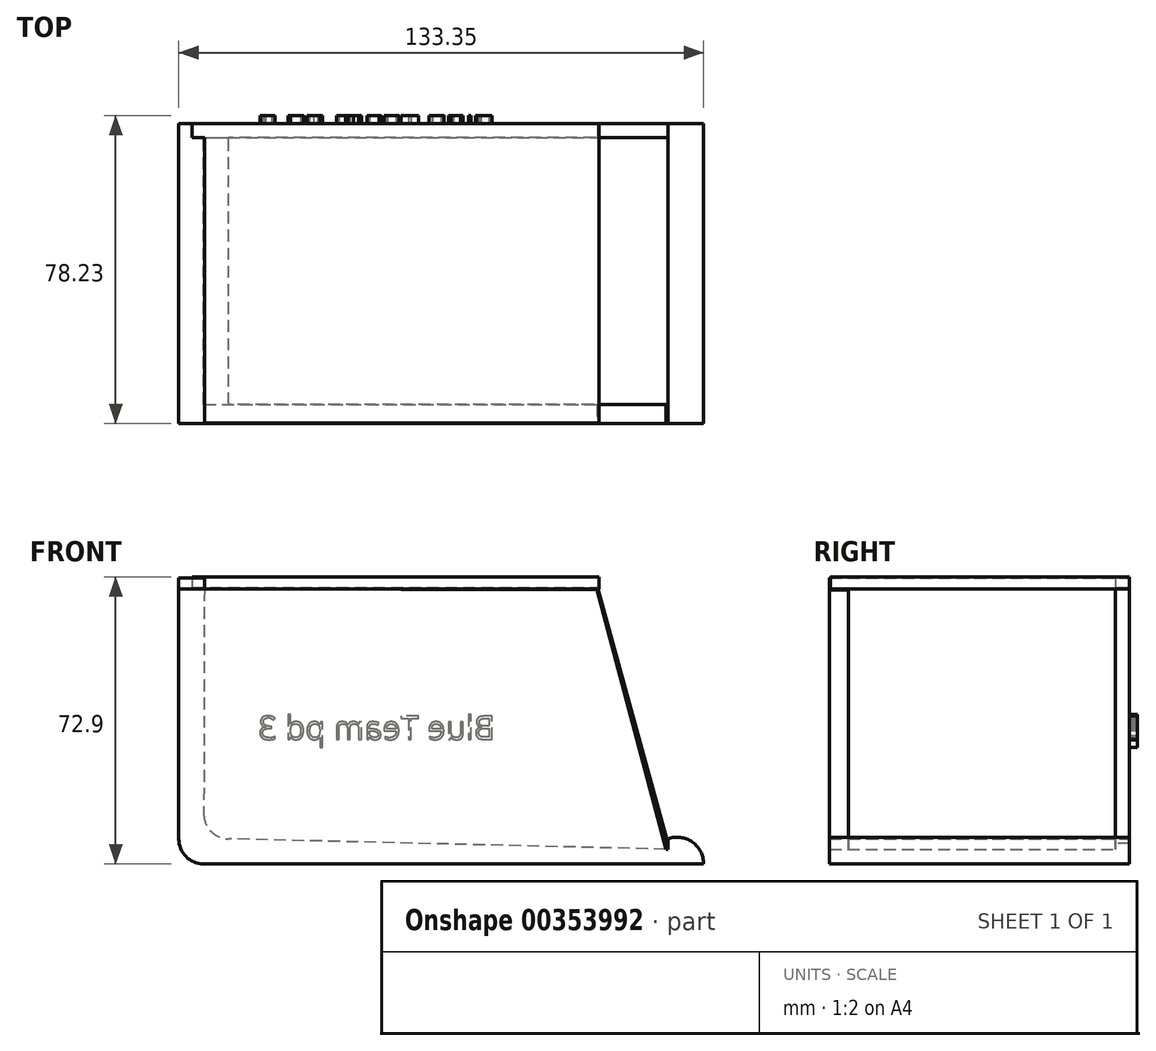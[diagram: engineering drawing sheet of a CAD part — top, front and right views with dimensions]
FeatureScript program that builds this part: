
annotation { "Feature Type Name" : "Feature", "Feature Type Description" : "" }
export const myFeature = defineFeature(function(context is Context, id is Id, definition is map)
    precondition{}
    {
        {
            var Q0;
            Q0=qCreatedBy(makeId("Front.planeOp"),FACE);
            var sketch = newSketch(context, id + "F0", { "sketchPlane" : qUnion([Q0])});
            skLineSegment(sketch, "E0", {"start": v(-20.46, 51.98) * mm, "end": v(-20.46, -11.52) * mm});
            skLineSegment(sketch, "E1", {"start": v(-14.1, -17.87) * mm, "end": v(112.9, -17.87) * mm});
            skPoint(sketch, "E2.visualSharp", {"position": v(-20.46, -17.87) * mm});
            skArc(sketch, "E2.filletArc", {"start": v(-20.46, -11.52) * mm, "mid": v(-18.6, -16) * mm, "end": v(-14.1, -17.87) * mm});
            skLineSegment(sketch, "E3", {"start": v(-20.46, 51.98) * mm, "end": v(-13.95, 51.98) * mm});
            skLineSegment(sketch, "E4", {"start": v(-13.95, 51.98) * mm, "end": v(-14.1, -5.15) * mm});
            skLineSegment(sketch, "E5", {"start": v(112.9, -17.87) * mm, "end": v(112.9, -17.87) * mm});
            skArc(sketch, "E6.filletArc", {"start": v(-14.1, -5.15) * mm, "mid": v(-12.24, -9.65) * mm, "end": v(-7.74, -11.52) * mm});
            skArc(sketch, "E7", {"start": v(112.9, -17.87) * mm, "mid": v(110, -12.31) * mm, "end": v(103.78, -11.52) * mm});
            skLineSegment(sketch, "E8", {"start": v(103.78, -11.52) * mm, "end": v(103.78, -14.16) * mm});
            skLineSegment(sketch, "E9", {"start": v(103.78, -14.16) * mm, "end": v(-7.74, -11.52) * mm});
            skLineSegment(sketch, "E10", {"start": v(-13.95, 51.98) * mm, "end": v(60.84, 51.8) * mm});
            skLineSegment(sketch, "E11", {"start": v(60.84, 51.8) * mm, "end": v(83.04, 51.8) * mm});
            skLineSegment(sketch, "E12", {"start": v(83.04, 51.8) * mm, "end": v(103.78, -11.52) * mm});
            skSolve(sketch);
        }
        {
            var Q0;
            Q0=makeQuery(id+"F0.imprint","IMPRINT",FACE,{"disambiguationData":[TD([[makeQuery(id+"F0.imprint","IMPRINT",EDGE,{"derivedFrom":sQuery(id+"F0.wireOp",EDGE,"E0")}),1.0]])]});
            extrude(context, id + "F1", {"entities" : qUnion([Q0]), "depth" : 76.2 * mm});
        }
        {
            var Q0;
            Q0=qCreatedBy(makeId("Front.planeOp"),FACE);
            var sketch = newSketch(context, id + "F2", { "sketchPlane" : qUnion([Q0])});
            skLineSegment(sketch, "E13", {"start": v(-17.13, 52.33) * mm, "end": v(86, 52.33) * mm});
            skLineSegment(sketch, "E14", {"start": v(86, 52.33) * mm, "end": v(104.33, -14.69) * mm});
            skLineSegment(sketch, "E15", {"start": v(104.33, -14.69) * mm, "end": v(-17.06, -13.08) * mm});
            skLineSegment(sketch, "E16", {"start": v(-17.06, -13.08) * mm, "end": v(-17.13, 52.33) * mm});
            skSolve(sketch);
        }
        {
            var Q0;
            Q0=makeQuery(id+"F2.imprint","IMPRINT",FACE,{"disambiguationData":[TD([[makeQuery(id+"F2.imprint","IMPRINT",EDGE,{"derivedFrom":sQuery(id+"F2.wireOp",EDGE,"E13")}),-1.0]])]});
            extrude(context, id + "F3", {"entities" : qUnion([Q0]), "operationType" : NewBodyOperationType.ADD, "depth" : 3.56 * mm});
        }
        {
            var Q0;
            Q0=makeQuery(id+"F1.opExtrude","CAP_FACE",FACE,{"disambiguationData":[OSD([sQuery(id+"F0.wireOp",EDGE,"E0"),sQuery(id+"F0.wireOp",EDGE,"E1"),sQuery(id+"F0.wireOp",EDGE,"E2.filletArc"),sQuery(id+"F0.wireOp",EDGE,"E3"),sQuery(id+"F0.wireOp",EDGE,"E4"),sQuery(id+"F0.wireOp",EDGE,"E6.filletArc"),sQuery(id+"F0.wireOp",EDGE,"E7"),sQuery(id+"F0.wireOp",EDGE,"E8"),sQuery(id+"F0.wireOp",EDGE,"E9")])],"isStart":false});
            var sketch = newSketch(context, id + "F4", { "sketchPlane" : qUnion([Q0])});
            skLineSegment(sketch, "E17", {"start": v(-13.95, 51.98) * mm, "end": v(85.84, 51.75) * mm});
            skLineSegment(sketch, "E18", {"start": v(85.84, 51.75) * mm, "end": v(103.78, -15.92) * mm});
            skLineSegment(sketch, "E19", {"start": v(103.78, -15.92) * mm, "end": v(-16.75, -14.16) * mm});
            skLineSegment(sketch, "E20", {"start": v(-16.75, -14.16) * mm, "end": v(-15.84, 48.68) * mm});
            skLineSegment(sketch, "E21", {"start": v(-15.84, 48.68) * mm, "end": v(-13.95, 51.98) * mm});
            skSolve(sketch);
        }
        {
            var Q0;
            {var subQ4=sQuery(id+"F4.wireOp",EDGE,"E19");Q0=makeQuery(id+"F4.imprint","IMPRINT",FACE,{"disambiguationData":[TD([[makeQuery(id+"F4.imprint","IMPRINT",EDGE,{"derivedFrom":subQ4}),-1.0]])]});}
            extrude(context, id + "F5", {"entities" : qUnion([Q0]), "operationType" : NewBodyOperationType.ADD, "oppositeDirection" : true, "depth" : 5.33 * mm});
        }
        {
            var Q0;
            Q0 = qSketchRegion(id + "F4", true);
            extrude(context, id + "F6", {"entities" : qUnion([Q0]), "operationType" : NewBodyOperationType.ADD, "oppositeDirection" : true, "depth" : 4.83 * mm});
        }
        {
            var Q0;
            Q0=makeQuery(id+"F1.opExtrude","SWEPT_FACE",FACE,{"disambiguationData":[OSD([sQuery(id+"F0.wireOp",EDGE,"E3")])]});
            var sketch = newSketch(context, id + "F7", { "sketchPlane" : qUnion([Q0])});
            skLineSegment(sketch, "E22.bottom", {"start": v(-20.46, 0) * mm, "end": v(86.3, 0) * mm});
            skLineSegment(sketch, "E22.top", {"start": v(-20.46, -76.03) * mm, "end": v(86.3, -76.03) * mm});
            skLineSegment(sketch, "E22.left", {"start": v(-20.46, 0) * mm, "end": v(-20.46, -76.03) * mm});
            skLineSegment(sketch, "E22.right", {"start": v(86.3, 0) * mm, "end": v(86.3, -76.03) * mm});
            skSolve(sketch);
        }
        {
            var Q0;
            {var subQ4=sQuery(id+"F7.wireOp",EDGE,"E22.right");Q0=makeQuery(id+"F7.imprint","IMPRINT",FACE,{"disambiguationData":[TD([[makeQuery(id+"F7.imprint","IMPRINT",EDGE,{"derivedFrom":subQ4}),-1.0]])]});}
            extrude(context, id + "F8", {"entities" : qUnion([Q0]), "depth" : 3.05 * mm});
        }
        {
            var Q0;
            Q0=makeQuery(id+"F1.opExtrude","SWEPT_FACE",FACE,{"disambiguationData":[OSD([sQuery(id+"F0.wireOp",EDGE,"E3")])]});
            extrude(context, id + "F9", {"entities" : qUnion([Q0]), "depth" : 2.8 * mm});
        }
        {
            var Q0;
            Q0=makeQuery(id+"F3.boolean.opBoolean","MERGE",FACE,{"derivedFrom":[makeQuery(id+"F1.opExtrude","CAP_FACE",FACE,{"disambiguationData":[OSD([sQuery(id+"F0.wireOp",EDGE,"E0"),sQuery(id+"F0.wireOp",EDGE,"E1"),sQuery(id+"F0.wireOp",EDGE,"E2.filletArc"),sQuery(id+"F0.wireOp",EDGE,"E3"),sQuery(id+"F0.wireOp",EDGE,"E4"),sQuery(id+"F0.wireOp",EDGE,"E6.filletArc"),sQuery(id+"F0.wireOp",EDGE,"E7"),sQuery(id+"F0.wireOp",EDGE,"E8"),sQuery(id+"F0.wireOp",EDGE,"E9")])],"isStart":true}),makeQuery(id+"F3.opExtrude","CAP_FACE",FACE,{"disambiguationData":[OSD([sQuery(id+"F2.wireOp",EDGE,"E13"),sQuery(id+"F2.wireOp",EDGE,"E14"),sQuery(id+"F2.wireOp",EDGE,"E15"),sQuery(id+"F2.wireOp",EDGE,"E16")])],"isStart":true})]});
            var sketch = newSketch(context, id + "F10", { "sketchPlane" : qUnion([Q0])});
            skText(sketch, "E23", { "text": "Blue Team pd 3", "fontName": "OpenSans-Regular.ttf"});
            const initialGuessF10  = {"E23": [-0.05993, 0.01376, 1, 0, 0.00598]};
            skSetInitialGuess(sketch, initialGuessF10);
            skSolve(sketch);
        }
        {
            var Q0;
            Q0 = qSketchRegion(id + "F10", true);
            extrude(context, id + "F11", {"entities" : qUnion([Q0]), "operationType" : NewBodyOperationType.ADD, "depth" : 2.03 * mm});
        }
    });
